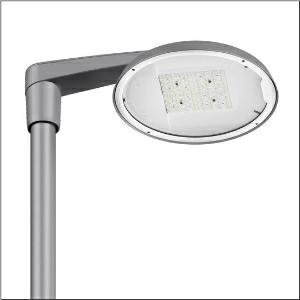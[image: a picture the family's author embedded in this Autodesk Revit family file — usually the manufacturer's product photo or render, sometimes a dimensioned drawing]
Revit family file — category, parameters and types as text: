
# Revit family: dl_r__50_iq_mini___st0_5a_5xa248b31f08ne_6eba
name_source: partatom
category: Lighting Fixtures
units: mm (PartAtom-declared; Revit-internal decimal feet)

## family parameters
Cut with Voids When Loaded = No
Host = Face
Light Source = No
Part Type = Normal
Room Calculation Point = No
Round Connector Dimension = Use Diameter
Shared = No

## types (1)
- --- (1 x LED, 19270 lm, 121.8 W, 3000K)
    Apparent Load = 122 VA
    CIE Flux Codes = 43 76 97 100 100
    Color Rendering = 70
    Color Temperature = 3000K
    Default Elevation = 1800 mm
    Description = DL® 50 iQ mini, mast luminaire, primary light control with lens, of PMMA, primary optical cover: cover, of toughened safety glass, transparent, light distribution: ST0.5a, light emission: direct distribution, primary light characteristic: asymmetric, installation type: side-entry, post-top, LED, High Power LED, rated luminous flux: 19.270lm, luminous efficacy: 158lm/W, light colour: 730, colour temperature: 3000K, control: optimised constant luminous flux control (CLO 2.0), Desk-Remote (wireless, voltage-free reading and setting of iQ features in the workshop via application-optimized NFC function/RFID function), Light-Fading, Smart-Wire, Night-Set, Lumen-Switch, Temp-Guard, Auto-Match, Street-Remote, mains connection: 230..240V, AC, 50/60Hz, connection cable pre-assembled, cable length: 10,5m, start of lifetime: 122W, end of service life: 134W, reduction: 55W, luminaire housing, of diecast aluminium, powder-coated, Siteco® metallic grey (DB 702S), inclination adjustable: 0°, 5°, 10° (post-top) | 0°, -5°, -10°, -15° (side-entry), please order mast post-top element or mast side-entry element separately, diameter: 500mm, height: 115mm, post-top: for spigot size d x l = 76 x 100mm; with reducer (optional accessory) 60 x 100mm | side-entry: for spigot size d x l = 60 x 100mm; with reducer (optional accessory) 42 x 100mm, protection rating (complete): IP66, insulation class (complete): insulation class II (safety insulation), certification: CE, ENEC, VDE, impact resistance: IK08, permissible operating ambient temperature for outdoor applications: -25..+40°C, standard-compliant lighting for roads and squares, packaging unit: 1 piece

Light Distribution: ST0.5a
    Height = 115 mm
    Lamp = 1 x LED
    Lamp Light Flux = 19270 lm
    Lamp Power = 121.8 W
    Lamp count = 1
    Length = 500 mm
    Luminous efficacy = 158 lm/W
    Manufacturer = Siteco
    ModVariant = No
    Model = 5XA248B31F08NE
    Number of Poles = 1
    OnlyDefault = Yes
    Power Factor = 1
    Product Name = DL® 50 iQ mini | ST0.5a
    Product group = mast luminaire | pylon top
    ProductGroupID = 6100
    Protection Class = Protection class II
    Protection Degree = IP 66
    RLX_Detail_Level = 1
    RLX_Emergency_Light_Flux = 0 lm
    RLX_Emergency_Type = 0
    RLX_Emergency_Type_DB = No
    RlxData = <blob elided: 128225 chars, md5=3ff1bcf7>
    Socket = socket
    Standby Power = 0 W
    System Light Flux = 19270 lm
    System Power = 122 W
    Type Comments = factory setting: luminous flux: 100 % | dim-lin: 254 | 657 mA
    Type Image = l_1251790.jpg
    URL = http://relux.com
    VarID = @adj_092213
    Voltage = 0 V
    Weight = 0.00 kg
    Width = 0 mm  [stored 0 ft]

note: [stored X ft] marks values corroborated as IEEE doubles in the binary element streams (Revit-internal decimal feet)

## geometry (parser evidence)
native form markers: Blend x4, Sweep x12
no freeform markers — native parametric forms only
